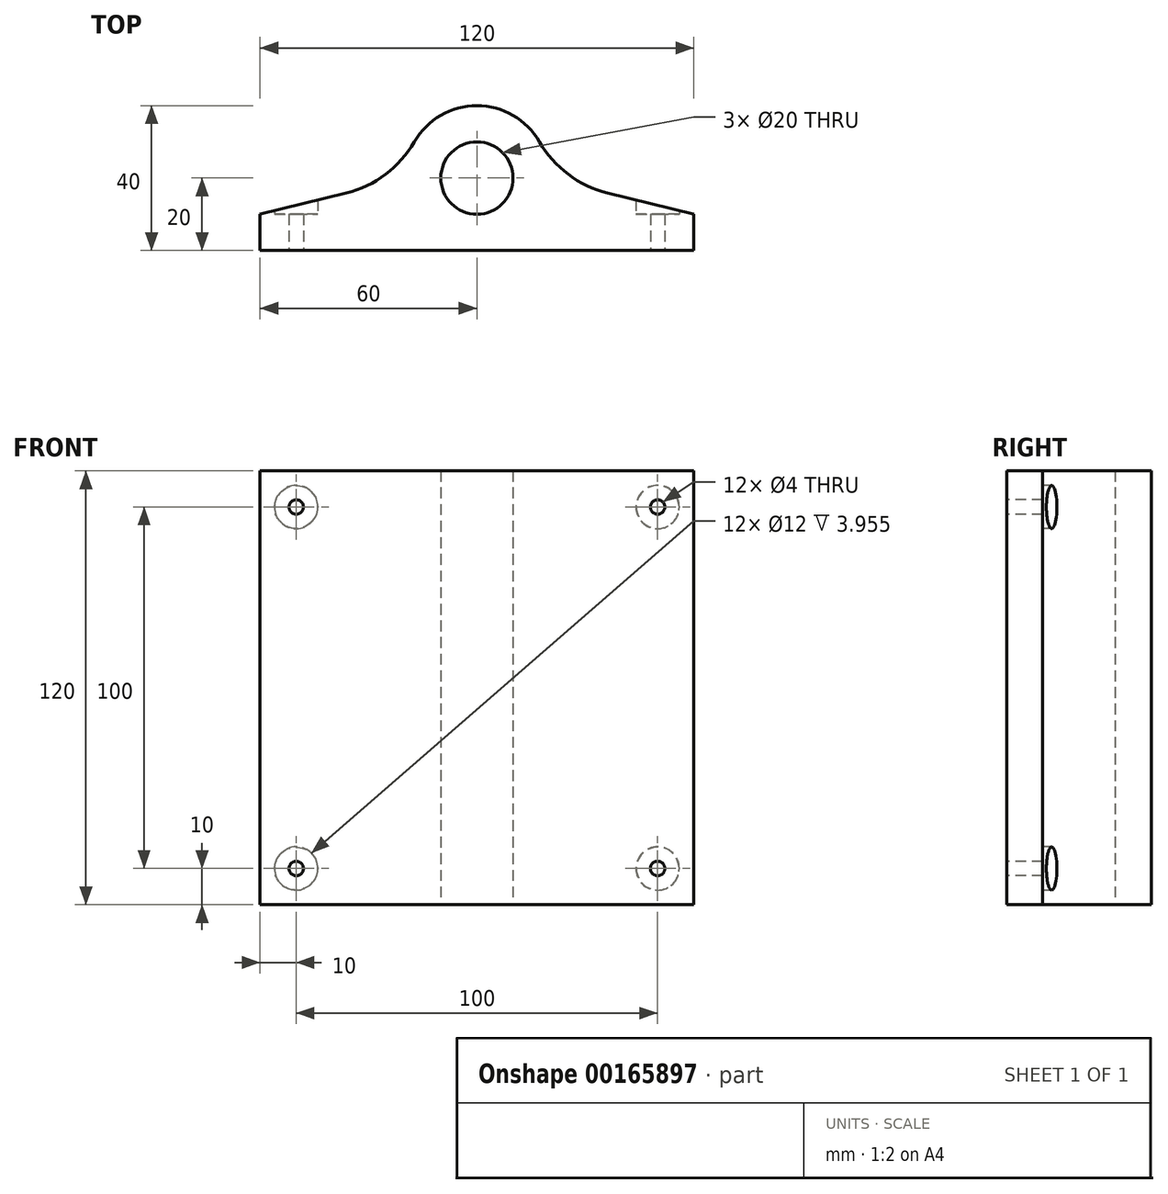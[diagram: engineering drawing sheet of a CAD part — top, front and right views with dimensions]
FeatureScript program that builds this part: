
annotation { "Feature Type Name" : "Feature", "Feature Type Description" : "" }
export const myFeature = defineFeature(function(context is Context, id is Id, definition is map)
    precondition{}
    {
        {
            var Q0;
            Q0=qCreatedBy(makeId("Top.planeOp"),FACE);
            var sketch = newSketch(context, id + "F0", { "sketchPlane" : qUnion([Q0])});
            skLineSegment(sketch, "E0", {"start": v(-60, 0) * mm, "end": v(0, 0) * mm});
            skLineSegment(sketch, "E1", {"start": v(-60, 0) * mm, "end": v(-60, 10) * mm});
            skCircle(sketch, "E2", {"center": v(0, 20) * mm, "radius": 10 * mm});
            skPoint(sketch, "E3", {"position": v(0, 10) * mm});
            skArc(sketch, "E4", {"start": v(0, 40) * mm, "mid": v(-10, 37.32) * mm, "end": v(-17.32, 30) * mm});
            skPoint(sketch, "E5", {"position": v(0, 30) * mm});
            skArc(sketch, "E6", {"start": v(-36.14, 15.87) * mm, "mid": v(-25.29, 21.01) * mm, "end": v(-17.32, 30) * mm});
            skLineSegment(sketch, "E7", {"start": v(-60, 10) * mm, "end": v(-36.14, 15.87) * mm});
            skArc(sketch, "E8.MirrorCS", {"start": v(0, 40) * mm, "mid": v(10, 37.32) * mm, "end": v(17.32, 30) * mm});
            skArc(sketch, "E9.MirrorCS", {"start": v(36.14, 15.87) * mm, "mid": v(25.29, 21.01) * mm, "end": v(17.32, 30) * mm});
            skLineSegment(sketch, "E10.MirrorCS", {"start": v(60, 10) * mm, "end": v(36.14, 15.87) * mm});
            skLineSegment(sketch, "E11.MirrorCS", {"start": v(60, 0) * mm, "end": v(60, 10) * mm});
            skLineSegment(sketch, "E12.MirrorCS", {"start": v(60, 0) * mm, "end": v(0, 0) * mm});
            skSolve(sketch);
        }
        {
            var Q0;
            Q0 = qSketchRegion(id + "F0", true);
            extrude(context, id + "F1", {"entities" : qUnion([Q0]), "depth" : 60 * mm, "hasSecondDirection" : true, "secondDirectionOppositeDirection" : true, "secondDirectionDepth" : 60 * mm});
        }
        {
            var Q0;
            Q0=makeQuery(id+"F1.opExtrude","SWEPT_FACE",FACE,{"disambiguationData":[OSD([sQuery(id+"F0.wireOp",EDGE,"E0"),sQuery(id+"F0.wireOp",EDGE,"E12.MirrorCS")])]});
            var sketch = newSketch(context, id + "F2", { "sketchPlane" : qUnion([Q0])});
            skCircle(sketch, "E13", {"center": v(-50, 50) * mm, "radius": 2 * mm});
            skCircle(sketch, "E14.MirrorC", {"center": v(50, 50) * mm, "radius": 2 * mm});
            skCircle(sketch, "E15.MirrorC", {"center": v(-50, -50) * mm, "radius": 2 * mm});
            skCircle(sketch, "E16.MirrorC", {"center": v(50, -50) * mm, "radius": 2 * mm});
            skLineSegment(sketch, "E17", {"start": v(-50, -50) * mm, "end": v(-50, 50) * mm, "construction": true});
            skLineSegment(sketch, "E18", {"start": v(-50, 50) * mm, "end": v(50, 50) * mm, "construction": true});
            skSolve(sketch);
        }
        {
            var Q0;
            Q0 = qSketchRegion(id + "F2", true);
            extrude(context, id + "F3", {"entities" : qUnion([Q0]), "operationType" : NewBodyOperationType.REMOVE, "oppositeDirection" : true, "depth" : 25 * mm});
        }
        {
            var Q0;
            Q0=makeQuery(id+"F1.opExtrude","SWEPT_FACE",FACE,{"disambiguationData":[OSD([sQuery(id+"F0.wireOp",EDGE,"E0"),sQuery(id+"F0.wireOp",EDGE,"E12.MirrorCS")])]});
            var sketch = newSketch(context, id + "F4", { "sketchPlane" : qUnion([Q0])});
            skCircle(sketch, "E19", {"center": v(-50, 50) * mm, "radius": 6 * mm});
            skCircle(sketch, "E20.MirrorC", {"center": v(50, -50) * mm, "radius": 6 * mm});
            skCircle(sketch, "E21.MirrorC", {"center": v(-50, -50) * mm, "radius": 6 * mm});
            skCircle(sketch, "E22.MirrorC", {"center": v(50, 50) * mm, "radius": 6 * mm});
            skSolve(sketch);
        }
        {
            var Q0;
            Q0 = qSketchRegion(id + "F4", true);
            extrude(context, id + "F5", {"entities" : qUnion([Q0]), "operationType" : NewBodyOperationType.REMOVE, "oppositeDirection" : true, "depth" : 25 * mm, "hasSecondDirection" : true, "secondDirectionOppositeDirection" : true, "secondDirectionDepth" : 10 * mm});
        }
    });
